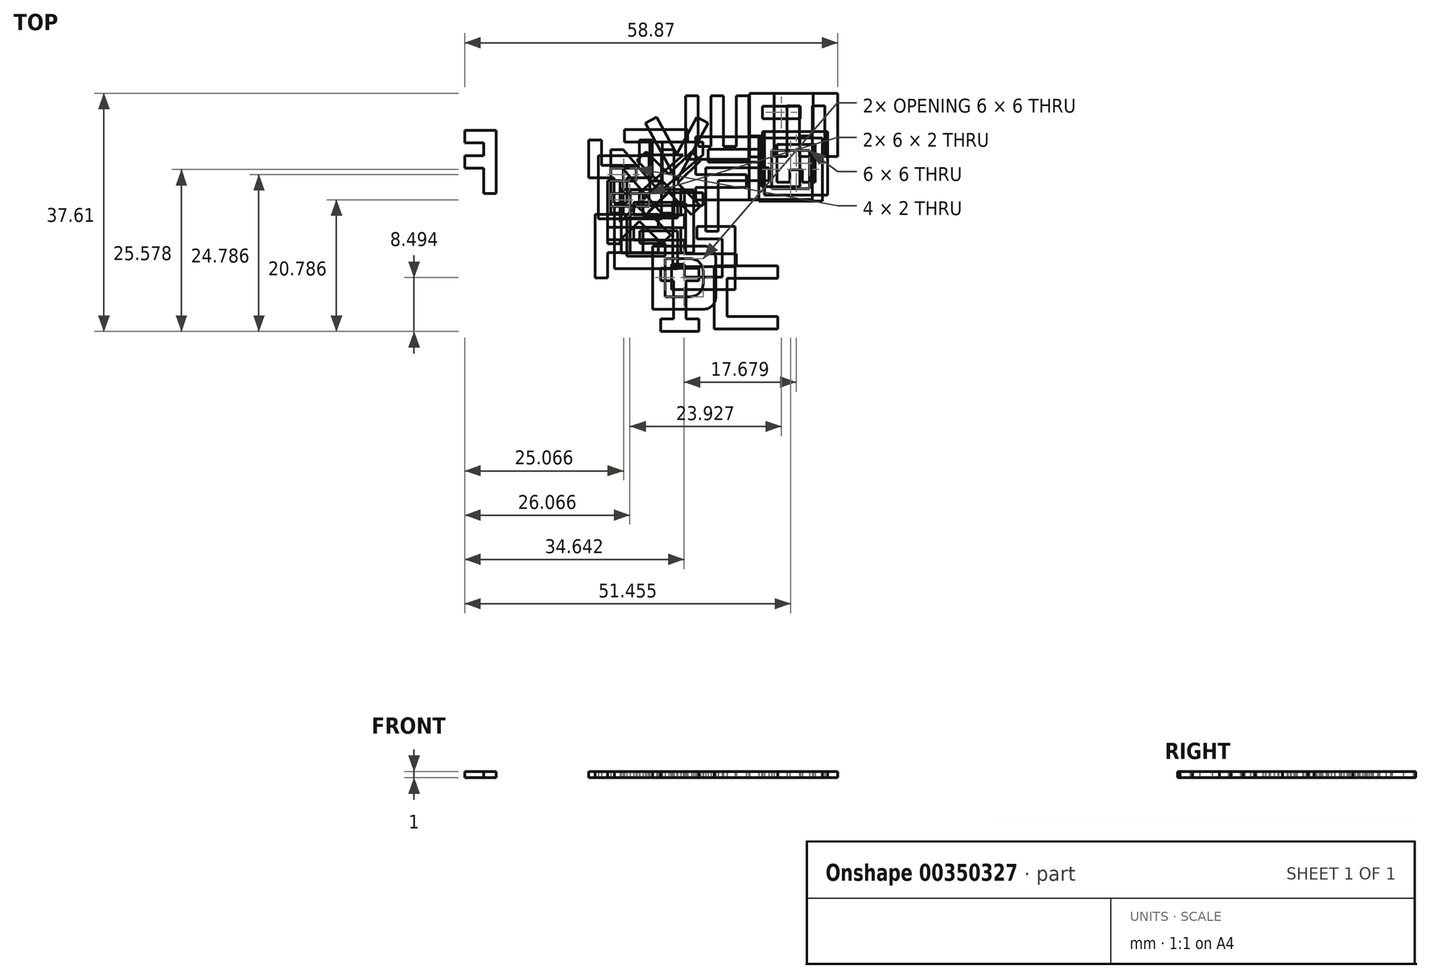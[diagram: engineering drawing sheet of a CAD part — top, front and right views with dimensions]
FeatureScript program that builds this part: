
annotation { "Feature Type Name" : "Feature", "Feature Type Description" : "" }
export const myFeature = defineFeature(function(context is Context, id is Id, definition is map)
    precondition{}
    {
        {
            var Q0;
            Q0=qCreatedBy(makeId("Top.planeOp"),FACE);
            var sketch = newSketch(context, id + "F0", { "sketchPlane" : qUnion([Q0])});
            skLineSegment(sketch, "E0.left", {"start": v(-30.22, 13.34) * mm, "end": v(-30.22, 3.34) * mm});
            skLineSegment(sketch, "E1", {"start": v(-30.22, 11.34) * mm, "end": v(-30.22, 3.34) * mm});
            skLineSegment(sketch, "E2", {"start": v(-30.22, 3.34) * mm, "end": v(-28.22, 3.34) * mm});
            skLineSegment(sketch, "E3", {"start": v(-25.22, 13.34) * mm, "end": v(-25.22, 3.34) * mm});
            skLineSegment(sketch, "E4", {"start": v(-30.22, 11.34) * mm, "end": v(-30.22, 13.34) * mm});
            skLineSegment(sketch, "E5", {"start": v(-28.22, 11.34) * mm, "end": v(-25.22, 11.34) * mm});
            skLineSegment(sketch, "E6", {"start": v(-28.22, 3.34) * mm, "end": v(-28.22, 7.34) * mm});
            skLineSegment(sketch, "E7", {"start": v(-28.22, 7.34) * mm, "end": v(-25.22, 7.34) * mm});
            skLineSegment(sketch, "E8", {"start": v(-28.22, 11.34) * mm, "end": v(-28.22, 9.34) * mm});
            skLineSegment(sketch, "E9", {"start": v(-28.22, 9.34) * mm, "end": v(-25.22, 9.34) * mm});
            skLineSegment(sketch, "E10.MirrorCS", {"start": v(-22.22, 9.34) * mm, "end": v(-25.22, 9.34) * mm});
            skLineSegment(sketch, "E11.MirrorCS", {"start": v(-22.22, 11.34) * mm, "end": v(-25.22, 11.34) * mm});
            skLineSegment(sketch, "E12.MirrorCS", {"start": v(-22.22, 11.34) * mm, "end": v(-22.22, 9.34) * mm});
            skLineSegment(sketch, "E13.MirrorCS", {"start": v(-22.22, 7.34) * mm, "end": v(-25.22, 7.34) * mm});
            skLineSegment(sketch, "E14.MirrorCS", {"start": v(-22.22, 3.34) * mm, "end": v(-22.22, 7.34) * mm});
            skLineSegment(sketch, "E15.MirrorCS", {"start": v(-20.22, 3.34) * mm, "end": v(-22.22, 3.34) * mm});
            skLineSegment(sketch, "E16.MirrorCS", {"start": v(-20.22, 11.34) * mm, "end": v(-20.22, 3.34) * mm});
            skLineSegment(sketch, "E17.MirrorCS", {"start": v(-20.22, 11.34) * mm, "end": v(-20.22, 13.34) * mm});
            skLineSegment(sketch, "E18", {"start": v(-30.22, 13.34) * mm, "end": v(-20.22, 13.34) * mm});
            skSolve(sketch);
        }
        {
            var Q0;
            Q0=makeQuery(id+"F0.imprint","IMPRINT",FACE,{"disambiguationData":[TD([[makeQuery(id+"F0.imprint","IMPRINT",EDGE,{"derivedFrom":sQuery(id+"F0.wireOp",EDGE,"E1")}),1.0]])]});
            var Q1;
            {var subQ6=sQuery(id+"F0.wireOp",EDGE,"E10.MirrorCS");Q1=makeQuery(id+"F0.imprint","IMPRINT",FACE,{"disambiguationData":[TD([[makeQuery(id+"F0.imprint","IMPRINT",EDGE,{"derivedFrom":subQ6}),1.0]])]});}
            extrude(context, id + "F1", {"entities" : qUnion([Q0, Q1]), "depth" : 1 * mm});
        }
        {
            var Q0;
            Q0=qCreatedBy(makeId("Top.planeOp"),FACE);
            var sketch = newSketch(context, id + "F2", { "sketchPlane" : qUnion([Q0])});
            skLineSegment(sketch, "E19.bottom", {"start": v(-4.15, 9.37) * mm, "end": v(3.85, 9.37) * mm});
            skLineSegment(sketch, "E19.top", {"start": v(-4.15, -0.63) * mm, "end": v(5.85, -0.63) * mm});
            skLineSegment(sketch, "E19.left", {"start": v(-4.15, 9.37) * mm, "end": v(-4.15, -0.63) * mm});
            skLineSegment(sketch, "E19.right", {"start": v(5.85, 5.37) * mm, "end": v(5.85, -0.63) * mm});
            skLineSegment(sketch, "E20", {"start": v(3.85, 9.37) * mm, "end": v(3.85, 5.37) * mm});
            skLineSegment(sketch, "E21", {"start": v(1.85, 5.37) * mm, "end": v(-2.15, 5.37) * mm});
            skLineSegment(sketch, "E22", {"start": v(-2.15, 5.37) * mm, "end": v(-2.15, 7.37) * mm});
            skLineSegment(sketch, "E23", {"start": v(-2.15, 7.37) * mm, "end": v(1.85, 7.37) * mm});
            skLineSegment(sketch, "E24", {"start": v(1.85, 7.37) * mm, "end": v(1.85, 5.37) * mm});
            skLineSegment(sketch, "E25", {"start": v(3.85, 5.37) * mm, "end": v(5.85, 5.37) * mm});
            skLineSegment(sketch, "E26", {"start": v(-2.15, 3.37) * mm, "end": v(3.85, 3.37) * mm});
            skLineSegment(sketch, "E27", {"start": v(3.85, 3.37) * mm, "end": v(3.85, 1.37) * mm});
            skLineSegment(sketch, "E28", {"start": v(3.85, 1.37) * mm, "end": v(-2.15, 1.37) * mm});
            skLineSegment(sketch, "E29", {"start": v(-2.15, 1.37) * mm, "end": v(-2.15, 3.37) * mm});
            skSolve(sketch);
        }
        {
            var Q0;
            Q0=makeQuery(id+"F2.imprint","IMPRINT",FACE,{"disambiguationData":[TD([[makeQuery(id+"F2.imprint","IMPRINT",EDGE,{"derivedFrom":sQuery(id+"F2.wireOp",EDGE,"E19.top")}),1.0]])]});
            extrude(context, id + "F3", {"entities" : qUnion([Q0]), "depth" : 1 * mm});
        }
        {
            var Q0;
            Q0=qCreatedBy(makeId("Top.planeOp"),FACE);
            var sketch = newSketch(context, id + "F4", { "sketchPlane" : qUnion([Q0])});
            skLineSegment(sketch, "E30.bottom", {"start": v(14.16, -8.04) * mm, "end": v(24.16, -8.04) * mm});
            skLineSegment(sketch, "E30.top", {"start": v(14.16, -18.04) * mm, "end": v(24.16, -18.04) * mm});
            skLineSegment(sketch, "E30.left", {"start": v(14.16, -8.04) * mm, "end": v(14.16, -18.04) * mm});
            skLineSegment(sketch, "E30.right", {"start": v(24.16, -8.04) * mm, "end": v(24.16, -10.04) * mm});
            skLineSegment(sketch, "E31", {"start": v(24.16, -10.04) * mm, "end": v(16.16, -10.04) * mm});
            skLineSegment(sketch, "E32", {"start": v(16.16, -10.04) * mm, "end": v(16.16, -16.04) * mm});
            skLineSegment(sketch, "E33", {"start": v(16.16, -16.04) * mm, "end": v(24.16, -16.04) * mm});
            skLineSegment(sketch, "E34.trimOffspring", {"start": v(24.16, -16.04) * mm, "end": v(24.16, -18.04) * mm});
            skSolve(sketch);
        }
        {
            var Q0;
            Q0=makeQuery(id+"F4.imprint","IMPRINT",FACE,{"disambiguationData":[TD([[makeQuery(id+"F4.imprint","IMPRINT",EDGE,{"derivedFrom":sQuery(id+"F4.wireOp",EDGE,"E30.bottom")}),-1.0]])]});
            extrude(context, id + "F5", {"entities" : qUnion([Q0]), "depth" : 1 * mm});
        }
        {
            var Q0;
            Q0=qCreatedBy(makeId("Top.planeOp"),FACE);
            var sketch = newSketch(context, id + "F6", { "sketchPlane" : qUnion([Q0])});
            skLineSegment(sketch, "E35.bottom", {"start": v(4.42, -4.93) * mm, "end": v(12.42, -4.93) * mm});
            skLineSegment(sketch, "E35.top", {"start": v(4.42, -14.93) * mm, "end": v(12.42, -14.93) * mm});
            skLineSegment(sketch, "E35.left", {"start": v(4.42, -4.93) * mm, "end": v(4.42, -14.93) * mm});
            skLineSegment(sketch, "E35.right", {"start": v(14.42, -6.93) * mm, "end": v(14.42, -12.93) * mm});
            skLineSegment(sketch, "E36", {"start": v(4.42, -4.93) * mm, "end": v(6.42, -4.93) * mm});
            skLineSegment(sketch, "E37", {"start": v(6.42, -6.93) * mm, "end": v(10.42, -6.93) * mm});
            skLineSegment(sketch, "E38", {"start": v(12.42, -8.93) * mm, "end": v(12.42, -10.93) * mm});
            skLineSegment(sketch, "E39", {"start": v(10.42, -12.93) * mm, "end": v(6.42, -12.93) * mm});
            skLineSegment(sketch, "E40", {"start": v(6.42, -12.93) * mm, "end": v(6.42, -6.93) * mm});
            skArc(sketch, "E41", {"start": v(12.42, -14.93) * mm, "mid": v(13.84, -14.34) * mm, "end": v(14.42, -12.93) * mm});
            skArc(sketch, "E42", {"start": v(10.42, -12.93) * mm, "mid": v(11.84, -12.34) * mm, "end": v(12.42, -10.93) * mm});
            skLineSegment(sketch, "E43", {"start": v(14.42, -9.93) * mm, "end": v(4.42, -10) * mm});
            skArc(sketch, "E44", {"start": v(12.42, -8.93) * mm, "mid": v(11.84, -7.51) * mm, "end": v(10.42, -6.93) * mm});
            skArc(sketch, "E45", {"start": v(14.42, -6.93) * mm, "mid": v(13.84, -5.51) * mm, "end": v(12.42, -4.93) * mm});
            skPoint(sketch, "E46.orphan", {"position": v(14.42, -4.93) * mm});
            skPoint(sketch, "E47.orphan", {"position": v(14.42, -14.93) * mm});
            skSolve(sketch);
        }
        {
            var Q0;
            Q0=makeQuery(id+"F6.imprint","IMPRINT",FACE,{"disambiguationData":[TD([[makeQuery(id+"F6.imprint","IMPRINT",EDGE,{"derivedFrom":sQuery(id+"F6.wireOp",EDGE,"E35.bottom")}),-1.0]])]});
            var Q1;
            {var subQ8=sQuery(id+"F6.wireOp",EDGE,"E35.top");Q1=makeQuery(id+"F6.imprint","IMPRINT",FACE,{"disambiguationData":[TD([[makeQuery(id+"F6.imprint","IMPRINT",EDGE,{"derivedFrom":subQ8}),1.0]])]});}
            extrude(context, id + "F7", {"entities" : qUnion([Q0, Q1]), "depth" : 1 * mm});
        }
        {
            var Q0;
            Q0=qCreatedBy(makeId("Top.planeOp"),FACE);
            var sketch = newSketch(context, id + "F8", { "sketchPlane" : qUnion([Q0])});
            skLineSegment(sketch, "E48.bottom", {"start": v(-0.51, 4) * mm, "end": v(9.49, 4) * mm});
            skLineSegment(sketch, "E48.top", {"start": v(-0.51, -6) * mm, "end": v(9.49, -6) * mm});
            skLineSegment(sketch, "E48.left", {"start": v(-0.51, 4) * mm, "end": v(-0.51, -6) * mm});
            skLineSegment(sketch, "E48.right", {"start": v(9.49, 4) * mm, "end": v(9.49, 2) * mm});
            skLineSegment(sketch, "E49", {"start": v(9.49, 2) * mm, "end": v(1.49, 2) * mm});
            skLineSegment(sketch, "E50", {"start": v(9.49, -6) * mm, "end": v(9.49, -4) * mm});
            skLineSegment(sketch, "E51", {"start": v(9.49, -4) * mm, "end": v(1.49, -4) * mm});
            skLineSegment(sketch, "E52", {"start": v(1.49, -4) * mm, "end": v(1.49, -2) * mm});
            skLineSegment(sketch, "E53", {"start": v(1.49, -2) * mm, "end": v(9.49, -2) * mm});
            skLineSegment(sketch, "E54", {"start": v(9.49, -2) * mm, "end": v(9.49, 0) * mm});
            skLineSegment(sketch, "E55", {"start": v(1.49, 2) * mm, "end": v(1.49, 0) * mm});
            skLineSegment(sketch, "E56", {"start": v(1.49, 0) * mm, "end": v(9.49, 0) * mm});
            skLineSegment(sketch, "E57.trimOffspring", {"start": v(9.49, 0) * mm, "end": v(9.49, -2) * mm});
            skLineSegment(sketch, "E58.trimOffspring", {"start": v(9.49, -4) * mm, "end": v(9.49, -6) * mm});
            skSolve(sketch);
        }
        {
            var Q0;
            Q0=makeQuery(id+"F8.imprint","IMPRINT",FACE,{"disambiguationData":[TD([[makeQuery(id+"F8.imprint","IMPRINT",EDGE,{"derivedFrom":sQuery(id+"F8.wireOp",EDGE,"E48.bottom")}),-1.0]])]});
            extrude(context, id + "F9", {"entities" : qUnion([Q0]), "depth" : 1 * mm});
        }
        {
            var Q0;
            Q0=qCreatedBy(makeId("Top.planeOp"),FACE);
            var sketch = newSketch(context, id + "F10", { "sketchPlane" : qUnion([Q0])});
            skLineSegment(sketch, "E59.bottom", {"start": v(-4.64, 0.06) * mm, "end": v(5.36, 0.06) * mm});
            skLineSegment(sketch, "E59.top", {"start": v(-4.64, -9.94) * mm, "end": v(-2.64, -9.94) * mm});
            skLineSegment(sketch, "E59.left", {"start": v(-4.64, 0.06) * mm, "end": v(-4.64, -9.94) * mm});
            skLineSegment(sketch, "E59.right", {"start": v(5.36, 0.06) * mm, "end": v(5.36, -1.94) * mm});
            skLineSegment(sketch, "E60", {"start": v(5.36, -1.94) * mm, "end": v(-2.64, -1.94) * mm});
            skLineSegment(sketch, "E61", {"start": v(-2.64, -1.94) * mm, "end": v(-2.64, -3.94) * mm});
            skLineSegment(sketch, "E62", {"start": v(-2.64, -3.94) * mm, "end": v(5.36, -3.94) * mm});
            skLineSegment(sketch, "E63", {"start": v(5.36, -3.94) * mm, "end": v(5.36, -5.94) * mm});
            skLineSegment(sketch, "E64", {"start": v(5.36, -5.94) * mm, "end": v(-2.64, -5.94) * mm});
            skLineSegment(sketch, "E65", {"start": v(-2.64, -5.94) * mm, "end": v(-2.64, -9.94) * mm});
            skSolve(sketch);
        }
        {
            var Q0;
            Q0=makeQuery(id+"F10.imprint","IMPRINT",FACE,{"disambiguationData":[TD([[makeQuery(id+"F10.imprint","IMPRINT",EDGE,{"derivedFrom":sQuery(id+"F10.wireOp",EDGE,"E59.bottom")}),-1.0]])]});
            extrude(context, id + "F11", {"entities" : qUnion([Q0]), "depth" : 1 * mm});
        }
        {
            var Q0;
            Q0=qCreatedBy(makeId("Top.planeOp"),FACE);
            var sketch = newSketch(context, id + "F12", { "sketchPlane" : qUnion([Q0])});
            skLineSegment(sketch, "E66.bottom", {"start": v(-1.61, 1.5) * mm, "end": v(8.39, 1.5) * mm});
            skLineSegment(sketch, "E66.top", {"start": v(-1.61, -8.5) * mm, "end": v(8.39, -8.5) * mm});
            skLineSegment(sketch, "E66.left", {"start": v(-1.61, 1.5) * mm, "end": v(-1.61, -8.5) * mm});
            skLineSegment(sketch, "E66.right", {"start": v(8.39, 1.5) * mm, "end": v(8.39, -0.5) * mm});
            skLineSegment(sketch, "E67", {"start": v(8.39, -0.5) * mm, "end": v(0.39, -0.5) * mm});
            skLineSegment(sketch, "E68", {"start": v(0.39, -0.5) * mm, "end": v(0.39, -6.5) * mm});
            skLineSegment(sketch, "E69", {"start": v(0.39, -6.5) * mm, "end": v(6.39, -6.5) * mm});
            skLineSegment(sketch, "E70", {"start": v(6.39, -6.5) * mm, "end": v(6.39, -4.5) * mm});
            skLineSegment(sketch, "E71", {"start": v(6.39, -4.5) * mm, "end": v(2.39, -4.5) * mm});
            skLineSegment(sketch, "E72", {"start": v(2.39, -4.5) * mm, "end": v(2.39, -2.5) * mm});
            skLineSegment(sketch, "E73", {"start": v(2.39, -2.5) * mm, "end": v(8.39, -2.5) * mm});
            skLineSegment(sketch, "E74.trimOffspring", {"start": v(8.39, -2.5) * mm, "end": v(8.39, -8.5) * mm});
            skSolve(sketch);
        }
        {
            var Q0;
            Q0=makeQuery(id+"F12.imprint","IMPRINT",FACE,{"disambiguationData":[TD([[makeQuery(id+"F12.imprint","IMPRINT",EDGE,{"derivedFrom":sQuery(id+"F12.wireOp",EDGE,"E66.bottom")}),-1.0]])]});
            extrude(context, id + "F13", {"entities" : qUnion([Q0]), "depth" : 1 * mm});
        }
        {
            var Q0;
            Q0=qCreatedBy(makeId("Top.planeOp"),FACE);
            var sketch = newSketch(context, id + "F14", { "sketchPlane" : qUnion([Q0])});
            skLineSegment(sketch, "E75.bottom", {"start": v(0.9, 3.95) * mm, "end": v(2.9, 3.95) * mm});
            skLineSegment(sketch, "E75.top", {"start": v(0.9, -6.05) * mm, "end": v(2.9, -6.05) * mm});
            skLineSegment(sketch, "E75.left", {"start": v(0.9, 3.95) * mm, "end": v(0.9, -6.05) * mm});
            skLineSegment(sketch, "E75.right", {"start": v(10.9, 3.95) * mm, "end": v(10.9, -6.05) * mm});
            skLineSegment(sketch, "E76", {"start": v(2.9, 3.95) * mm, "end": v(2.9, -0.05) * mm});
            skLineSegment(sketch, "E77", {"start": v(2.9, -0.05) * mm, "end": v(8.9, -0.05) * mm});
            skLineSegment(sketch, "E78", {"start": v(8.9, -0.05) * mm, "end": v(8.9, 3.95) * mm});
            skLineSegment(sketch, "E79", {"start": v(2.9, -6.05) * mm, "end": v(2.9, -2.05) * mm});
            skLineSegment(sketch, "E80", {"start": v(2.9, -2.05) * mm, "end": v(8.9, -2.05) * mm});
            skLineSegment(sketch, "E81", {"start": v(8.9, -2.05) * mm, "end": v(8.9, -6.05) * mm});
            skLineSegment(sketch, "E82.trimOffspring", {"start": v(8.9, -6.05) * mm, "end": v(10.9, -6.05) * mm});
            skLineSegment(sketch, "E83.trimOffspring", {"start": v(8.9, 3.95) * mm, "end": v(10.9, 3.95) * mm});
            skSolve(sketch);
        }
        {
            var Q0;
            Q0 = qSketchRegion(id + "F14", true);
            extrude(context, id + "F15", {"entities" : qUnion([Q0]), "depth" : 1 * mm});
        }
        {
            var Q0;
            Q0=qCreatedBy(makeId("Top.planeOp"),FACE);
            var sketch = newSketch(context, id + "F16", { "sketchPlane" : qUnion([Q0])});
            skLineSegment(sketch, "E84.bottom", {"start": v(5.73, -8.42) * mm, "end": v(11.73, -8.42) * mm});
            skLineSegment(sketch, "E84.top", {"start": v(5.73, -18.42) * mm, "end": v(11.73, -18.42) * mm});
            skLineSegment(sketch, "E85", {"start": v(5.73, -8.42) * mm, "end": v(5.73, -10.42) * mm});
            skLineSegment(sketch, "E86", {"start": v(5.73, -10.42) * mm, "end": v(7.73, -10.42) * mm});
            skLineSegment(sketch, "E87", {"start": v(7.73, -10.42) * mm, "end": v(7.73, -16.42) * mm});
            skLineSegment(sketch, "E88", {"start": v(7.73, -16.42) * mm, "end": v(5.73, -16.42) * mm});
            skLineSegment(sketch, "E89", {"start": v(5.73, -16.42) * mm, "end": v(5.73, -18.42) * mm});
            skLineSegment(sketch, "E90", {"start": v(8.73, -8.42) * mm, "end": v(8.73, -18.42) * mm});
            skLineSegment(sketch, "E91.MirrorCS", {"start": v(11.73, -8.42) * mm, "end": v(11.73, -10.42) * mm});
            skLineSegment(sketch, "E92.MirrorCS", {"start": v(11.73, -10.42) * mm, "end": v(9.73, -10.42) * mm});
            skLineSegment(sketch, "E93.MirrorCS", {"start": v(9.73, -10.42) * mm, "end": v(9.73, -16.42) * mm});
            skLineSegment(sketch, "E94.MirrorCS", {"start": v(9.73, -16.42) * mm, "end": v(11.73, -16.42) * mm});
            skLineSegment(sketch, "E95.MirrorCS", {"start": v(11.73, -16.42) * mm, "end": v(11.73, -18.42) * mm});
            skPoint(sketch, "E96.orphan", {"position": v(13.73, -8.42) * mm});
            skPoint(sketch, "E97.orphan", {"position": v(13.73, -18.42) * mm});
            skPoint(sketch, "E98.orphan", {"position": v(3.73, -18.42) * mm});
            skPoint(sketch, "E99.orphan", {"position": v(3.73, -8.42) * mm});
            skSolve(sketch);
        }
        {
            var Q0;
            {var subQ1=sQuery(id+"F16.wireOp",EDGE,"E90");Q0=makeQuery(id+"F16.imprint","IMPRINT",FACE,{"disambiguationData":[TD([[makeQuery(id+"F16.imprint","IMPRINT",EDGE,{"derivedFrom":subQ1}),1.0]])]});}
            var Q1;
            {var subQ0=sQuery(id+"F16.wireOp",EDGE,"E85");Q1=makeQuery(id+"F16.imprint","IMPRINT",FACE,{"disambiguationData":[TD([[makeQuery(id+"F16.imprint","IMPRINT",EDGE,{"derivedFrom":subQ0}),1.0]])]});}
            extrude(context, id + "F17", {"entities" : qUnion([Q0, Q1]), "depth" : 1 * mm});
        }
        {
            var Q0;
            Q0=qCreatedBy(makeId("Top.planeOp"),FACE);
            var sketch = newSketch(context, id + "F18", { "sketchPlane" : qUnion([Q0])});
            skLineSegment(sketch, "E100.bottom", {"start": v(11.45, -1.81) * mm, "end": v(17.45, -1.81) * mm});
            skLineSegment(sketch, "E100.top", {"start": v(7.45, -11.81) * mm, "end": v(17.45, -11.81) * mm});
            skLineSegment(sketch, "E100.left", {"start": v(7.45, -7.81) * mm, "end": v(7.45, -11.81) * mm});
            skLineSegment(sketch, "E100.right", {"start": v(17.45, -1.81) * mm, "end": v(17.45, -11.81) * mm});
            skLineSegment(sketch, "E101", {"start": v(17.45, -1.81) * mm, "end": v(17.45, -3.81) * mm});
            skLineSegment(sketch, "E102", {"start": v(17.45, -1.81) * mm, "end": v(11.45, -1.81) * mm});
            skLineSegment(sketch, "E103", {"start": v(11.45, -1.81) * mm, "end": v(11.45, -3.81) * mm});
            skLineSegment(sketch, "E104", {"start": v(11.45, -3.81) * mm, "end": v(15.45, -3.81) * mm});
            skLineSegment(sketch, "E105", {"start": v(15.45, -3.81) * mm, "end": v(15.45, -9.81) * mm});
            skLineSegment(sketch, "E106", {"start": v(15.45, -9.81) * mm, "end": v(9.45, -9.81) * mm});
            skLineSegment(sketch, "E107", {"start": v(9.45, -9.81) * mm, "end": v(9.45, -7.81) * mm});
            skLineSegment(sketch, "E108", {"start": v(9.45, -7.81) * mm, "end": v(7.45, -7.81) * mm});
            skSolve(sketch);
        }
        {
            var Q0;
            Q0=makeQuery(id+"F18.imprint","IMPRINT",FACE,{"disambiguationData":[TD([[makeQuery(id+"F18.imprint","IMPRINT",EDGE,{"derivedFrom":sQuery(id+"F18.wireOp",EDGE,"E100.top")}),1.0]])]});
            extrude(context, id + "F19", {"entities" : qUnion([Q0]), "depth" : 1 * mm});
        }
        {
            var Q0;
            Q0=qCreatedBy(makeId("Top.planeOp"),FACE);
            var sketch = newSketch(context, id + "F20", { "sketchPlane" : qUnion([Q0])});
            skLineSegment(sketch, "E109.bottom", {"start": v(-2.68, 5.42) * mm, "end": v(-0.68, 5.42) * mm});
            skLineSegment(sketch, "E109.top", {"start": v(-2.68, -4.58) * mm, "end": v(-0.68, -4.58) * mm});
            skLineSegment(sketch, "E109.left", {"start": v(-2.68, 5.42) * mm, "end": v(-2.68, -4.58) * mm});
            skLineSegment(sketch, "E110", {"start": v(-0.68, 5.42) * mm, "end": v(-0.68, -1.16) * mm});
            skLineSegment(sketch, "E111.0", {"start": v(7.32, -3.16) * mm, "end": v(3.74, 0.42) * mm});
            skLineSegment(sketch, "E112.0", {"start": v(5.91, -4.58) * mm, "end": v(2.32, -1) * mm});
            skLineSegment(sketch, "E113.0", {"start": v(5.91, 5.42) * mm, "end": v(-0.68, -1.16) * mm});
            skLineSegment(sketch, "E114.0", {"start": v(7.32, 4) * mm, "end": v(3.74, 0.42) * mm});
            skLineSegment(sketch, "E115", {"start": v(5.91, 5.42) * mm, "end": v(7.32, 4) * mm});
            skLineSegment(sketch, "E116", {"start": v(7.32, -3.16) * mm, "end": v(5.91, -4.58) * mm});
            skLineSegment(sketch, "E117.trimOffspring", {"start": v(2.32, -1) * mm, "end": v(-0.68, -4) * mm});
            skLineSegment(sketch, "E118.trimOffspring", {"start": v(-0.68, -4) * mm, "end": v(-0.68, -4.58) * mm});
            skSolve(sketch);
        }
        {
            var Q0;
            Q0=makeQuery(id+"F20.imprint","IMPRINT",FACE,{"disambiguationData":[TD([[makeQuery(id+"F20.imprint","IMPRINT",EDGE,{"derivedFrom":sQuery(id+"F20.wireOp",EDGE,"E109.top")}),1.0]])]});
            extrude(context, id + "F21", {"entities" : qUnion([Q0]), "depth" : 1 * mm});
        }
        {
            var Q0;
            Q0=qCreatedBy(makeId("Top.planeOp"),FACE);
            var sketch = newSketch(context, id + "F22", { "sketchPlane" : qUnion([Q0])});
            skLineSegment(sketch, "E119.bottom", {"start": v(7.65, 1.84) * mm, "end": v(9.65, 1.84) * mm});
            skLineSegment(sketch, "E119.top", {"start": v(7.65, -8.16) * mm, "end": v(17.65, -8.16) * mm});
            skLineSegment(sketch, "E119.left", {"start": v(7.65, 1.84) * mm, "end": v(7.65, -8.16) * mm});
            skLineSegment(sketch, "E119.right", {"start": v(17.65, -6.16) * mm, "end": v(17.65, -8.16) * mm});
            skLineSegment(sketch, "E120", {"start": v(9.65, 1.84) * mm, "end": v(9.65, -6.16) * mm});
            skLineSegment(sketch, "E121", {"start": v(9.65, -6.16) * mm, "end": v(17.65, -6.16) * mm});
            skSolve(sketch);
        }
        {
            var Q0;
            Q0=makeQuery(id+"F22.imprint","IMPRINT",FACE,{"disambiguationData":[TD([[makeQuery(id+"F22.imprint","IMPRINT",EDGE,{"derivedFrom":sQuery(id+"F22.wireOp",EDGE,"E119.top")}),1.0]])]});
            extrude(context, id + "F23", {"entities" : qUnion([Q0]), "depth" : 1 * mm});
        }
        {
            var Q0;
            Q0=qCreatedBy(makeId("Top.planeOp"),FACE);
            var sketch = newSketch(context, id + "F24", { "sketchPlane" : qUnion([Q0])});
            skLineSegment(sketch, "E122.bottom", {"start": v(23.65, 19.2) * mm, "end": v(33.65, 19.2) * mm});
            skLineSegment(sketch, "E122.top", {"start": v(23.65, 9.2) * mm, "end": v(25.65, 9.2) * mm});
            skLineSegment(sketch, "E122.left", {"start": v(23.65, 19.2) * mm, "end": v(23.65, 9.2) * mm});
            skLineSegment(sketch, "E122.right", {"start": v(33.65, 19.2) * mm, "end": v(33.65, 9.2) * mm});
            skLineSegment(sketch, "E123", {"start": v(25.65, 9.2) * mm, "end": v(25.65, 17.2) * mm});
            skLineSegment(sketch, "E124", {"start": v(25.65, 17.2) * mm, "end": v(27.65, 17.2) * mm});
            skLineSegment(sketch, "E125", {"start": v(27.65, 17.2) * mm, "end": v(27.65, 9.2) * mm});
            skLineSegment(sketch, "E126", {"start": v(27.65, 9.2) * mm, "end": v(29.65, 9.2) * mm});
            skLineSegment(sketch, "E127", {"start": v(29.65, 9.2) * mm, "end": v(29.65, 17.2) * mm});
            skLineSegment(sketch, "E128", {"start": v(29.65, 17.2) * mm, "end": v(31.65, 17.2) * mm});
            skLineSegment(sketch, "E129", {"start": v(31.65, 17.2) * mm, "end": v(31.65, 9.2) * mm});
            skLineSegment(sketch, "E130.trimOffspring", {"start": v(31.65, 9.2) * mm, "end": v(33.65, 9.2) * mm});
            skSolve(sketch);
        }
        {
            var Q0;
            Q0=makeQuery(id+"F24.imprint","IMPRINT",FACE,{"disambiguationData":[TD([[makeQuery(id+"F24.imprint","IMPRINT",EDGE,{"derivedFrom":sQuery(id+"F24.wireOp",EDGE,"E122.bottom")}),-1.0]])]});
            extrude(context, id + "F25", {"entities" : qUnion([Q0]), "depth" : 1 * mm});
        }
        {
            var Q0;
            Q0=qCreatedBy(makeId("Top.planeOp"),FACE);
            var sketch = newSketch(context, id + "F26", { "sketchPlane" : qUnion([Q0])});
            skLineSegment(sketch, "E131.bottom", {"start": v(-2.17, 10.28) * mm, "end": v(-0.17, 10.28) * mm});
            skLineSegment(sketch, "E131.top", {"start": v(-2.17, 0.28) * mm, "end": v(-0.17, 0.28) * mm});
            skLineSegment(sketch, "E131.left", {"start": v(-2.17, 10.28) * mm, "end": v(-2.17, 0.28) * mm});
            skLineSegment(sketch, "E131.right", {"start": v(7.83, 10.28) * mm, "end": v(7.83, 0.28) * mm});
            skLineSegment(sketch, "E132", {"start": v(-0.17, 0.28) * mm, "end": v(-0.17, 7.22) * mm});
            skLineSegment(sketch, "E133", {"start": v(7.83, 10.28) * mm, "end": v(5.83, 10.28) * mm});
            skLineSegment(sketch, "E134", {"start": v(5.83, 10.28) * mm, "end": v(5.83, 3.33) * mm});
            skLineSegment(sketch, "E135", {"start": v(5.83, 0.28) * mm, "end": v(-0.17, 7.22) * mm});
            skLineSegment(sketch, "E136", {"start": v(-0.17, 10.28) * mm, "end": v(5.83, 3.33) * mm});
            skLineSegment(sketch, "E137.trimOffspring", {"start": v(5.83, 10.28) * mm, "end": v(7.83, 10.28) * mm});
            skLineSegment(sketch, "E138.trimOffspring", {"start": v(5.83, 0.28) * mm, "end": v(7.83, 0.28) * mm});
            skSolve(sketch);
        }
        {
            var Q0;
            Q0=makeQuery(id+"F26.imprint","IMPRINT",FACE,{"disambiguationData":[TD([[makeQuery(id+"F26.imprint","IMPRINT",EDGE,{"derivedFrom":sQuery(id+"F26.wireOp",EDGE,"E131.bottom")}),-1.0]])]});
            extrude(context, id + "F27", {"entities" : qUnion([Q0]), "depth" : 1 * mm});
        }
        {
            var Q0;
            Q0=qCreatedBy(makeId("Top.planeOp"),FACE);
            var sketch = newSketch(context, id + "F28", { "sketchPlane" : qUnion([Q0])});
            skLineSegment(sketch, "E139.bottom", {"start": v(21.24, 12.16) * mm, "end": v(31.24, 12.16) * mm});
            skLineSegment(sketch, "E139.top", {"start": v(21.24, 2.16) * mm, "end": v(31.24, 2.16) * mm});
            skLineSegment(sketch, "E139.left", {"start": v(21.24, 12.16) * mm, "end": v(21.24, 2.16) * mm});
            skLineSegment(sketch, "E139.right", {"start": v(31.24, 12.16) * mm, "end": v(31.24, 2.16) * mm});
            skLineSegment(sketch, "E140", {"start": v(21.24, 12.16) * mm, "end": v(23.24, 12.16) * mm});
            skLineSegment(sketch, "E141", {"start": v(23.24, 10.16) * mm, "end": v(23.24, 4.16) * mm});
            skLineSegment(sketch, "E142", {"start": v(23.24, 4.16) * mm, "end": v(29.24, 4.16) * mm});
            skLineSegment(sketch, "E143", {"start": v(29.24, 4.16) * mm, "end": v(29.24, 10.16) * mm});
            skLineSegment(sketch, "E144", {"start": v(29.24, 10.16) * mm, "end": v(23.24, 10.16) * mm});
            skSolve(sketch);
        }
        {
            var Q0;
            Q0=makeQuery(id+"F28.imprint","IMPRINT",FACE,{"disambiguationData":[TD([[makeQuery(id+"F28.imprint","IMPRINT",EDGE,{"derivedFrom":sQuery(id+"F28.wireOp",EDGE,"E139.bottom")}),-1.0]])]});
            extrude(context, id + "F29", {"entities" : qUnion([Q0]), "depth" : 1 * mm});
        }
        {
            var Q0;
            Q0=qCreatedBy(makeId("Top.planeOp"),FACE);
            var sketch = newSketch(context, id + "F30", { "sketchPlane" : qUnion([Q0])});
            skLineSegment(sketch, "E145.bottom", {"start": v(19.77, 19.18) * mm, "end": v(29.77, 19.18) * mm});
            skLineSegment(sketch, "E145.left", {"start": v(19.77, 19.18) * mm, "end": v(19.77, 9.18) * mm});
            skLineSegment(sketch, "E145.right", {"start": v(29.77, 19.18) * mm, "end": v(29.77, 13.18) * mm});
            skLineSegment(sketch, "E146", {"start": v(19.77, 9.18) * mm, "end": v(21.77, 9.18) * mm});
            skLineSegment(sketch, "E147", {"start": v(21.77, 9.18) * mm, "end": v(21.77, 13.18) * mm});
            skLineSegment(sketch, "E148", {"start": v(21.77, 13.18) * mm, "end": v(29.77, 13.18) * mm});
            skLineSegment(sketch, "E149", {"start": v(21.77, 15.18) * mm, "end": v(21.77, 17.18) * mm});
            skLineSegment(sketch, "E150", {"start": v(21.77, 17.18) * mm, "end": v(27.77, 17.18) * mm});
            skLineSegment(sketch, "E151", {"start": v(27.77, 17.18) * mm, "end": v(27.77, 15.18) * mm});
            skLineSegment(sketch, "E152", {"start": v(27.77, 15.18) * mm, "end": v(21.77, 15.18) * mm});
            skSolve(sketch);
        }
        {
            var Q0;
            Q0=makeQuery(id+"F30.imprint","IMPRINT",FACE,{"disambiguationData":[TD([[makeQuery(id+"F30.imprint","IMPRINT",EDGE,{"derivedFrom":sQuery(id+"F30.wireOp",EDGE,"E145.bottom")}),-1.0]])]});
            extrude(context, id + "F31", {"entities" : qUnion([Q0]), "depth" : 1 * mm});
        }
        {
            var Q0;
            Q0=qCreatedBy(makeId("Top.planeOp"),FACE);
            var sketch = newSketch(context, id + "F32", { "sketchPlane" : qUnion([Q0])});
            skLineSegment(sketch, "E153.bottom", {"start": v(22.1, 13.14) * mm, "end": v(32.1, 13.14) * mm});
            skLineSegment(sketch, "E153.top", {"start": v(22.1, 3.14) * mm, "end": v(32.1, 3.14) * mm});
            skLineSegment(sketch, "E153.left", {"start": v(22.1, 13.14) * mm, "end": v(22.1, 3.14) * mm});
            skLineSegment(sketch, "E153.right", {"start": v(32.1, 13.14) * mm, "end": v(32.1, 3.14) * mm});
            skLineSegment(sketch, "E154", {"start": v(22.1, 3.14) * mm, "end": v(24.1, 3.14) * mm});
            skLineSegment(sketch, "E155", {"start": v(24.1, 5.14) * mm, "end": v(26.1, 5.14) * mm});
            skLineSegment(sketch, "E156", {"start": v(30.1, 5.14) * mm, "end": v(30.1, 11.14) * mm});
            skLineSegment(sketch, "E157", {"start": v(30.1, 11.14) * mm, "end": v(24.1, 11.14) * mm});
            skLineSegment(sketch, "E158", {"start": v(24.1, 11.14) * mm, "end": v(24.1, 5.14) * mm});
            skLineSegment(sketch, "E159", {"start": v(26.1, 5.14) * mm, "end": v(26.1, 7.14) * mm});
            skLineSegment(sketch, "E160", {"start": v(26.1, 7.14) * mm, "end": v(28.1, 7.14) * mm});
            skLineSegment(sketch, "E161", {"start": v(28.1, 7.14) * mm, "end": v(28.1, 5.14) * mm});
            skLineSegment(sketch, "E162.trimOffspring", {"start": v(28.1, 5.14) * mm, "end": v(30.1, 5.14) * mm});
            skSolve(sketch);
        }
        {
            var Q0;
            Q0=makeQuery(id+"F32.imprint","IMPRINT",FACE,{"disambiguationData":[TD([[makeQuery(id+"F32.imprint","IMPRINT",EDGE,{"derivedFrom":sQuery(id+"F32.wireOp",EDGE,"E153.bottom")}),-1.0]])]});
            extrude(context, id + "F33", {"entities" : qUnion([Q0]), "depth" : 1 * mm});
        }
        {
            var Q0;
            Q0=qCreatedBy(makeId("Top.planeOp"),FACE);
            var sketch = newSketch(context, id + "F34", { "sketchPlane" : qUnion([Q0])});
            skLineSegment(sketch, "E163.bottom", {"start": v(12.8, 7.41) * mm, "end": v(22.8, 7.41) * mm});
            skLineSegment(sketch, "E163.top", {"start": v(12.8, -2.59) * mm, "end": v(14.8, -2.59) * mm});
            skLineSegment(sketch, "E163.left", {"start": v(12.8, 7.41) * mm, "end": v(12.8, -2.59) * mm});
            skLineSegment(sketch, "E163.right", {"start": v(22.8, 7.41) * mm, "end": v(22.8, 5.41) * mm});
            skLineSegment(sketch, "E164", {"start": v(14.8, -2.59) * mm, "end": v(14.8, 5.41) * mm});
            skLineSegment(sketch, "E165", {"start": v(14.8, 5.41) * mm, "end": v(22.8, 5.41) * mm});
            skPoint(sketch, "E166.orphan", {"position": v(22.8, -2.59) * mm});
            skSolve(sketch);
        }
        {
            var Q0;
            Q0=makeQuery(id+"F34.imprint","IMPRINT",FACE,{"disambiguationData":[TD([[makeQuery(id+"F34.imprint","IMPRINT",EDGE,{"derivedFrom":sQuery(id+"F34.wireOp",EDGE,"E163.bottom")}),-1.0]])]});
            extrude(context, id + "F35", {"entities" : qUnion([Q0]), "depth" : 1 * mm});
        }
        {
            var Q0;
            Q0=qCreatedBy(makeId("Top.planeOp"),FACE);
            var sketch = newSketch(context, id + "F36", { "sketchPlane" : qUnion([Q0])});
            skLineSegment(sketch, "E167.bottom", {"start": v(11.22, 12.32) * mm, "end": v(21.22, 12.32) * mm});
            skLineSegment(sketch, "E167.top", {"start": v(11.22, 2.32) * mm, "end": v(21.22, 2.32) * mm});
            skLineSegment(sketch, "E167.left", {"start": v(11.22, 12.32) * mm, "end": v(11.22, 6.32) * mm});
            skLineSegment(sketch, "E167.right", {"start": v(21.22, 12.32) * mm, "end": v(21.22, 10.32) * mm});
            skLineSegment(sketch, "E168", {"start": v(21.22, 10.32) * mm, "end": v(13.22, 10.32) * mm});
            skLineSegment(sketch, "E169", {"start": v(13.22, 10.32) * mm, "end": v(13.22, 8.32) * mm});
            skLineSegment(sketch, "E170", {"start": v(13.22, 8.32) * mm, "end": v(21.22, 8.32) * mm});
            skLineSegment(sketch, "E171", {"start": v(11.22, 6.32) * mm, "end": v(19.22, 6.32) * mm});
            skLineSegment(sketch, "E172", {"start": v(19.22, 6.32) * mm, "end": v(19.22, 4.32) * mm});
            skLineSegment(sketch, "E173", {"start": v(19.22, 4.32) * mm, "end": v(11.22, 4.32) * mm});
            skLineSegment(sketch, "E174.trimOffspring", {"start": v(11.22, 4.32) * mm, "end": v(11.22, 2.32) * mm});
            skLineSegment(sketch, "E175.trimOffspring", {"start": v(21.22, 8.32) * mm, "end": v(21.22, 2.32) * mm});
            skSolve(sketch);
        }
        {
            var Q0;
            Q0=makeQuery(id+"F36.imprint","IMPRINT",FACE,{"disambiguationData":[TD([[makeQuery(id+"F36.imprint","IMPRINT",EDGE,{"derivedFrom":sQuery(id+"F36.wireOp",EDGE,"E167.bottom")}),-1.0]])]});
            extrude(context, id + "F37", {"entities" : qUnion([Q0]), "depth" : 1 * mm});
        }
        {
            var Q0;
            Q0=qCreatedBy(makeId("Top.planeOp"),FACE);
            var sketch = newSketch(context, id + "F38", { "sketchPlane" : qUnion([Q0])});
            skLineSegment(sketch, "E176.bottom", {"start": v(0, 13.5) * mm, "end": v(10, 13.5) * mm});
            skLineSegment(sketch, "E176.top", {"start": v(4, 3.5) * mm, "end": v(6, 3.5) * mm});
            skLineSegment(sketch, "E176.left", {"start": v(0, 13.5) * mm, "end": v(0, 11.5) * mm});
            skLineSegment(sketch, "E176.right", {"start": v(10, 13.5) * mm, "end": v(10, 11.5) * mm});
            skLineSegment(sketch, "E177", {"start": v(0, 11.5) * mm, "end": v(4, 11.5) * mm});
            skLineSegment(sketch, "E178", {"start": v(4, 11.5) * mm, "end": v(4, 3.5) * mm});
            skLineSegment(sketch, "E179", {"start": v(10, 11.5) * mm, "end": v(6, 11.5) * mm});
            skLineSegment(sketch, "E180", {"start": v(6, 11.5) * mm, "end": v(6, 3.5) * mm});
            skSolve(sketch);
        }
        {
            var Q0;
            Q0=makeQuery(id+"F38.imprint","IMPRINT",FACE,{"disambiguationData":[TD([[makeQuery(id+"F38.imprint","IMPRINT",EDGE,{"derivedFrom":sQuery(id+"F38.wireOp",EDGE,"E176.bottom")}),-1.0]])]});
            extrude(context, id + "F39", {"entities" : qUnion([Q0]), "depth" : 1 * mm});
        }
        {
            var Q0;
            Q0=qCreatedBy(makeId("Top.planeOp"),FACE);
            var sketch = newSketch(context, id + "F40", { "sketchPlane" : qUnion([Q0])});
            skLineSegment(sketch, "E181.bottom", {"start": v(19.68, 12.43) * mm, "end": v(21.68, 12.43) * mm});
            skLineSegment(sketch, "E181.top", {"start": v(19.68, 2.43) * mm, "end": v(29.68, 2.43) * mm});
            skLineSegment(sketch, "E181.left", {"start": v(19.68, 12.43) * mm, "end": v(19.68, 2.43) * mm});
            skLineSegment(sketch, "E181.right", {"start": v(29.68, 12.43) * mm, "end": v(29.68, 2.43) * mm});
            skLineSegment(sketch, "E182", {"start": v(21.68, 12.43) * mm, "end": v(21.68, 4.43) * mm});
            skLineSegment(sketch, "E183", {"start": v(21.68, 4.43) * mm, "end": v(27.68, 4.43) * mm});
            skLineSegment(sketch, "E184", {"start": v(27.68, 4.43) * mm, "end": v(27.68, 12.43) * mm});
            skLineSegment(sketch, "E185.trimOffspring", {"start": v(27.68, 12.43) * mm, "end": v(29.68, 12.43) * mm});
            skSolve(sketch);
        }
        {
            var Q0;
            Q0=makeQuery(id+"F40.imprint","IMPRINT",FACE,{"disambiguationData":[TD([[makeQuery(id+"F40.imprint","IMPRINT",EDGE,{"derivedFrom":sQuery(id+"F40.wireOp",EDGE,"E181.top")}),1.0]])]});
            extrude(context, id + "F41", {"entities" : qUnion([Q0]), "depth" : 1 * mm});
        }
        {
            var Q0;
            Q0=qCreatedBy(makeId("Top.planeOp"),FACE);
            var sketch = newSketch(context, id + "F42", { "sketchPlane" : qUnion([Q0])});
            skLineSegment(sketch, "E186", {"start": v(8.26, 5.41) * mm, "end": v(3.31, 14.45) * mm});
            skLineSegment(sketch, "E187", {"start": v(8.26, 9.58) * mm, "end": v(5.07, 15.41) * mm});
            skLineSegment(sketch, "E188", {"start": v(5.07, 15.41) * mm, "end": v(3.31, 14.45) * mm});
            skPoint(sketch, "E189.orphan", {"position": v(3.26, 15.41) * mm});
            skLineSegment(sketch, "E190.MirrorCS", {"start": v(8.26, 5.41) * mm, "end": v(13.2, 14.45) * mm});
            skLineSegment(sketch, "E191.MirrorCS", {"start": v(11.45, 15.41) * mm, "end": v(13.2, 14.45) * mm});
            skLineSegment(sketch, "E192.trimOffspring", {"start": v(8.26, 9.58) * mm, "end": v(8.26, 15.41) * mm});
            skLineSegment(sketch, "E193.trimOffspring", {"start": v(8.26, 9.58) * mm, "end": v(11.45, 15.41) * mm});
            skPoint(sketch, "E194.MirrorCS.start.orphan", {"position": v(6.5, 6.37) * mm});
            skPoint(sketch, "E195.end.orphan", {"position": v(9.14, 5.9) * mm});
            skPoint(sketch, "E196.orphan", {"position": v(10.01, 6.37) * mm});
            skPoint(sketch, "E197.orphan", {"position": v(3.26, 5.41) * mm});
            skPoint(sketch, "E198.right.end.orphan", {"position": v(13.26, 5.41) * mm});
            skPoint(sketch, "E198.bottom.end.orphan", {"position": v(13.26, 15.41) * mm});
            skSolve(sketch);
        }
        {
            var Q0;
            Q0=makeQuery(id+"F42.imprint","IMPRINT",FACE,{"disambiguationData":[TD([[makeQuery(id+"F42.imprint","IMPRINT",EDGE,{"derivedFrom":sQuery(id+"F42.wireOp",EDGE,"E186")}),-1.0]])]});
            extrude(context, id + "F43", {"entities" : qUnion([Q0]), "depth" : 1 * mm});
        }
        {
            var Q0;
            Q0=qCreatedBy(makeId("Top.planeOp"),FACE);
            var sketch = newSketch(context, id + "F44", { "sketchPlane" : qUnion([Q0])});
            skLineSegment(sketch, "E199.bottom", {"start": v(9.65, 18.78) * mm, "end": v(11.65, 18.78) * mm});
            skLineSegment(sketch, "E199.top", {"start": v(9.65, 8.78) * mm, "end": v(19.65, 8.78) * mm});
            skLineSegment(sketch, "E199.left", {"start": v(9.65, 18.78) * mm, "end": v(9.65, 8.78) * mm});
            skLineSegment(sketch, "E199.right", {"start": v(19.65, 18.78) * mm, "end": v(19.65, 8.78) * mm});
            skLineSegment(sketch, "E200", {"start": v(11.65, 18.78) * mm, "end": v(11.65, 10.78) * mm});
            skLineSegment(sketch, "E201", {"start": v(11.65, 10.78) * mm, "end": v(13.65, 10.78) * mm});
            skLineSegment(sketch, "E202", {"start": v(13.65, 10.78) * mm, "end": v(13.65, 18.78) * mm});
            skLineSegment(sketch, "E203", {"start": v(13.65, 18.78) * mm, "end": v(15.65, 18.78) * mm});
            skLineSegment(sketch, "E204", {"start": v(15.65, 18.78) * mm, "end": v(15.65, 10.78) * mm});
            skLineSegment(sketch, "E205", {"start": v(15.65, 10.78) * mm, "end": v(17.65, 10.78) * mm});
            skLineSegment(sketch, "E206", {"start": v(17.65, 10.78) * mm, "end": v(17.65, 18.78) * mm});
            skLineSegment(sketch, "E207.trimOffspring", {"start": v(17.65, 18.78) * mm, "end": v(19.65, 18.78) * mm});
            skSolve(sketch);
        }
        {
            var Q0;
            Q0=makeQuery(id+"F44.imprint","IMPRINT",FACE,{"disambiguationData":[TD([[makeQuery(id+"F44.imprint","IMPRINT",EDGE,{"derivedFrom":sQuery(id+"F44.wireOp",EDGE,"E199.top")}),1.0]])]});
            extrude(context, id + "F45", {"entities" : qUnion([Q0]), "depth" : 1 * mm});
        }
        {
            var Q0;
            Q0=qCreatedBy(makeId("Top.planeOp"),FACE);
            var sketch = newSketch(context, id + "F46", { "sketchPlane" : qUnion([Q0])});
            skLineSegment(sketch, "E208.0", {"start": v(3.41, 10) * mm, "end": v(7, 6.41) * mm});
            skLineSegment(sketch, "E209.0", {"start": v(3.41, 0) * mm, "end": v(7, 3.59) * mm});
            skLineSegment(sketch, "E210.0", {"start": v(2, 8.59) * mm, "end": v(5.59, 5) * mm});
            skLineSegment(sketch, "E211.0", {"start": v(2, 1.41) * mm, "end": v(5.59, 5) * mm});
            skLineSegment(sketch, "E212", {"start": v(3.41, 10) * mm, "end": v(2, 8.59) * mm});
            skLineSegment(sketch, "E213", {"start": v(2, 1.41) * mm, "end": v(3.41, 0) * mm});
            skLineSegment(sketch, "E214", {"start": v(10.59, 0) * mm, "end": v(12, 1.41) * mm});
            skLineSegment(sketch, "E215", {"start": v(12, 8.59) * mm, "end": v(10.59, 10) * mm});
            skPoint(sketch, "E216.orphan", {"position": v(12, 0) * mm});
            skLineSegment(sketch, "E217.trimOffspring", {"start": v(7, 6.41) * mm, "end": v(10.59, 10) * mm});
            skLineSegment(sketch, "E218.trimOffspring", {"start": v(7, 3.59) * mm, "end": v(10.59, 0) * mm});
            skLineSegment(sketch, "E219.trimOffspring", {"start": v(8.41, 5) * mm, "end": v(12, 8.59) * mm});
            skLineSegment(sketch, "E220.trimOffspring", {"start": v(8.41, 5) * mm, "end": v(12, 1.41) * mm});
            skSolve(sketch);
        }
        {
            var Q0;
            Q0=makeQuery(id+"F46.imprint","IMPRINT",FACE,{"disambiguationData":[TD([[makeQuery(id+"F46.imprint","IMPRINT",EDGE,{"derivedFrom":sQuery(id+"F46.wireOp",EDGE,"E208.0")}),-1.0]])]});
            extrude(context, id + "F47", {"entities" : qUnion([Q0]), "depth" : 1 * mm});
        }
        {
            var Q0;
            Q0=qCreatedBy(makeId("Top.planeOp"),FACE);
            var sketch = newSketch(context, id + "F48", { "sketchPlane" : qUnion([Q0])});
            skLineSegment(sketch, "E221.bottom", {"start": v(-5.64, 11.84) * mm, "end": v(-3.64, 11.84) * mm});
            skLineSegment(sketch, "E221.top", {"start": v(-1.64, 1.84) * mm, "end": v(0.36, 1.84) * mm});
            skLineSegment(sketch, "E221.left", {"start": v(-5.64, 11.84) * mm, "end": v(-5.64, 5.84) * mm});
            skLineSegment(sketch, "E221.right", {"start": v(4.36, 11.84) * mm, "end": v(4.36, 5.84) * mm});
            skLineSegment(sketch, "E222", {"start": v(-3.64, 11.84) * mm, "end": v(-3.64, 7.84) * mm});
            skLineSegment(sketch, "E223", {"start": v(-3.64, 7.84) * mm, "end": v(2.36, 7.84) * mm});
            skLineSegment(sketch, "E224", {"start": v(2.36, 7.84) * mm, "end": v(2.36, 11.84) * mm});
            skLineSegment(sketch, "E225", {"start": v(-5.64, 5.84) * mm, "end": v(-1.64, 5.84) * mm});
            skLineSegment(sketch, "E226", {"start": v(-1.64, 5.84) * mm, "end": v(-1.64, 1.84) * mm});
            skLineSegment(sketch, "E227", {"start": v(0.36, 1.84) * mm, "end": v(0.36, 5.84) * mm});
            skLineSegment(sketch, "E228", {"start": v(0.36, 5.84) * mm, "end": v(4.36, 5.84) * mm});
            skLineSegment(sketch, "E229.trimOffspring", {"start": v(2.36, 11.84) * mm, "end": v(4.36, 11.84) * mm});
            skSolve(sketch);
        }
        {
            var Q0;
            Q0=makeQuery(id+"F48.imprint","IMPRINT",FACE,{"disambiguationData":[TD([[makeQuery(id+"F48.imprint","IMPRINT",EDGE,{"derivedFrom":sQuery(id+"F48.wireOp",EDGE,"E221.right")}),-1.0]])]});
            extrude(context, id + "F49", {"entities" : qUnion([Q0]), "depth" : 1 * mm});
        }
        {
            var Q0;
            Q0=qCreatedBy(makeId("Top.planeOp"),FACE);
            var sketch = newSketch(context, id + "F50", { "sketchPlane" : qUnion([Q0])});
            skLineSegment(sketch, "E230.bottom", {"start": v(2.36, 11.5) * mm, "end": v(12.36, 11.5) * mm});
            skLineSegment(sketch, "E230.top", {"start": v(2.36, 1.5) * mm, "end": v(12.36, 1.5) * mm});
            skLineSegment(sketch, "E230.left", {"start": v(2.36, 11.5) * mm, "end": v(2.36, 9.5) * mm});
            skLineSegment(sketch, "E230.right", {"start": v(12.36, 11.5) * mm, "end": v(12.36, 9.5) * mm});
            skLineSegment(sketch, "E231", {"start": v(2.36, 9.5) * mm, "end": v(9.3, 9.5) * mm});
            skLineSegment(sketch, "E232", {"start": v(12.36, 1.5) * mm, "end": v(12.36, 3.5) * mm});
            skLineSegment(sketch, "E233", {"start": v(12.36, 3.5) * mm, "end": v(5.42, 3.5) * mm});
            skLineSegment(sketch, "E234", {"start": v(5.42, 3.5) * mm, "end": v(12.36, 9.5) * mm});
            skLineSegment(sketch, "E235", {"start": v(2.36, 3.5) * mm, "end": v(9.3, 9.5) * mm});
            skLineSegment(sketch, "E236.trimOffspring", {"start": v(12.36, 3.5) * mm, "end": v(12.36, 1.5) * mm});
            skLineSegment(sketch, "E237.trimOffspring", {"start": v(2.36, 3.5) * mm, "end": v(2.36, 1.5) * mm});
            skSolve(sketch);
        }
        {
            var Q0;
            Q0=makeQuery(id+"F50.imprint","IMPRINT",FACE,{"disambiguationData":[TD([[makeQuery(id+"F50.imprint","IMPRINT",EDGE,{"derivedFrom":sQuery(id+"F50.wireOp",EDGE,"E230.bottom")}),-1.0]])]});
            extrude(context, id + "F51", {"entities" : qUnion([Q0]), "depth" : 1 * mm});
        }
    });
